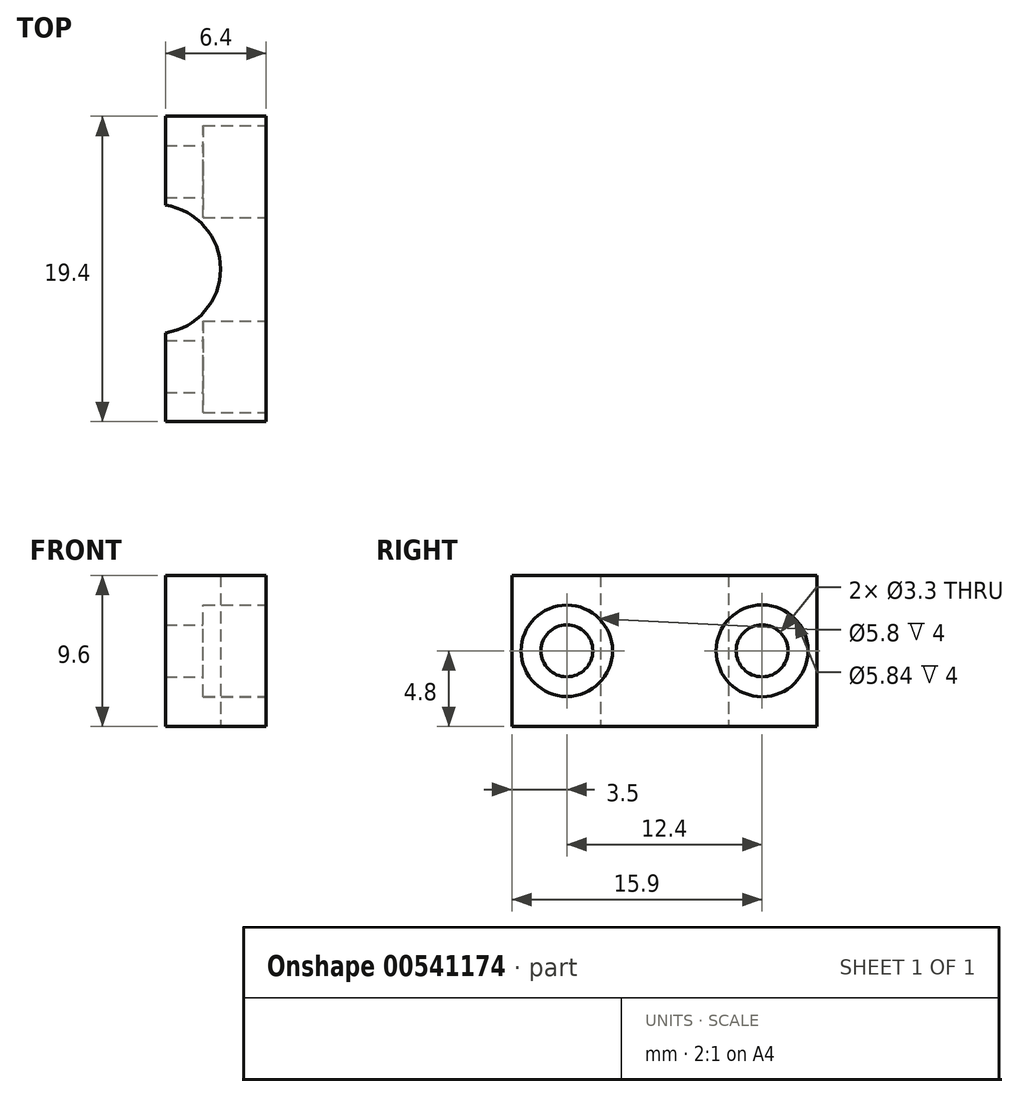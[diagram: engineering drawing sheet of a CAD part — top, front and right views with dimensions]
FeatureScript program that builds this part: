
annotation { "Feature Type Name" : "Feature", "Feature Type Description" : "" }
export const myFeature = defineFeature(function(context is Context, id is Id, definition is map)
    precondition{}
    {
        {
            var Q0;
            Q0=qCreatedBy(makeId("Top.planeOp"),FACE);
            var sketch = newSketch(context, id + "F0", { "sketchPlane" : qUnion([Q0])});
            skCircle(sketch, "E0", {"center": v(-7, 9.7) * mm, "radius": 4.1 * mm});
            skLineSegment(sketch, "E1", {"start": v(-7, 9.7) * mm, "end": v(-7, 35.1) * mm, "construction": true});
            skLineSegment(sketch, "E2", {"start": v(-7.6, 13.76) * mm, "end": v(-7.6, 19.7) * mm});
            skLineSegment(sketch, "E3", {"start": v(-7.6, 19.7) * mm, "end": v(-7, 19.7) * mm});
            skLineSegment(sketch, "E4.MirrorCS", {"start": v(-6.4, 19.7) * mm, "end": v(-7, 19.7) * mm});
            skLineSegment(sketch, "E5.MirrorCS", {"start": v(-6.4, 13.76) * mm, "end": v(-6.4, 19.7) * mm});
            skLineSegment(sketch, "E6", {"start": v(-6.4, 19.7) * mm, "end": v(0, 19.7) * mm});
            skLineSegment(sketch, "E7", {"start": v(0, 19.7) * mm, "end": v(0, 19.4) * mm});
            skLineSegment(sketch, "E8", {"start": v(0, 19.4) * mm, "end": v(-6.4, 19.4) * mm});
            skLineSegment(sketch, "E9", {"start": v(-7, 9.7) * mm, "end": v(-20.13, 9.7) * mm, "construction": true});
            skLineSegment(sketch, "E10.MirrorCS", {"start": v(-6.4, 5.64) * mm, "end": v(-6.4, -0.3) * mm});
            skLineSegment(sketch, "E11.MirrorCS", {"start": v(-7.6, 5.64) * mm, "end": v(-7.6, -0.3) * mm});
            skLineSegment(sketch, "E12.MirrorCS", {"start": v(0, 0) * mm, "end": v(-6.4, 0) * mm});
            skLineSegment(sketch, "E13.MirrorCS", {"start": v(-6.4, -0.3) * mm, "end": v(0, -0.3) * mm});
            skLineSegment(sketch, "E14.MirrorCS", {"start": v(0, -0.3) * mm, "end": v(0, 0) * mm});
            skLineSegment(sketch, "E15.MirrorCS", {"start": v(-6.4, -0.3) * mm, "end": v(-7, -0.3) * mm});
            skLineSegment(sketch, "E16.MirrorCS", {"start": v(-7.6, -0.3) * mm, "end": v(-7, -0.3) * mm});
            skLineSegment(sketch, "E17", {"start": v(0, 0) * mm, "end": v(0, 19.4) * mm});
            skSolve(sketch);
        }
        {
            var Q0;
            {var subQ0=sQuery(id+"F0.wireOp",EDGE,"E8");Q0=makeQuery(id+"F0.imprint","IMPRINT",FACE,{"disambiguationData":[TD([[makeQuery(id+"F0.imprint","IMPRINT",EDGE,{"derivedFrom":subQ0}),1.0]])]});}
            extrude(context, id + "F1", {"entities" : qUnion([Q0]), "depth" : 9.6 * mm, "offsetDistance" : 25 * mm});
        }
        {
            var Q0;
            Q0=qCreatedBy(makeId("Right.planeOp"),FACE);
            var sketch = newSketch(context, id + "F2", { "sketchPlane" : qUnion([Q0])});
            skCircle(sketch, "E18", {"center": v(15.9, 4.8) * mm, "radius": 1.65 * mm});
            skCircle(sketch, "E19", {"center": v(3.5, 4.8) * mm, "radius": 1.65 * mm});
            skPoint(sketch, "E20.0.midPoint", {"position": v(13, 4.8) * mm});
            skPoint(sketch, "E21.0.midPoint", {"position": v(0.6, 4.8) * mm});
            skCircle(sketch, "E22", {"center": v(15.9, 4.8) * mm, "radius": 2.92 * mm});
            skCircle(sketch, "E23", {"center": v(3.5, 4.8) * mm, "radius": 2.9 * mm});
            skSolve(sketch);
        }
        {
            var Q0;
            Q0=makeQuery(id+"F2.imprint","IMPRINT",FACE,{"disambiguationData":[TD([[makeQuery(id+"F2.imprint","IMPRINT",EDGE,{"derivedFrom":sQuery(id+"F2.wireOp",EDGE,"E19")}),1.0]])]});
            var Q1;
            Q1=makeQuery(id+"F2.imprint","IMPRINT",FACE,{"disambiguationData":[TD([[makeQuery(id+"F2.imprint","IMPRINT",EDGE,{"derivedFrom":sQuery(id+"F2.wireOp",EDGE,"E18")}),1.0]])]});
            extrude(context, id + "F3", {"entities" : qUnion([Q0, Q1]), "operationType" : NewBodyOperationType.REMOVE, "oppositeDirection" : true, "depth" : 25 * mm, "offsetDistance" : 25 * mm});
        }
        {
            var Q0;
            Q0=makeQuery(id+"F2.imprint","IMPRINT",FACE,{"disambiguationData":[TD([[makeQuery(id+"F2.imprint","IMPRINT",EDGE,{"derivedFrom":sQuery(id+"F2.wireOp",EDGE,"E19")}),-1.0]])]});
            var Q1;
            Q1=makeQuery(id+"F2.imprint","IMPRINT",FACE,{"disambiguationData":[TD([[makeQuery(id+"F2.imprint","IMPRINT",EDGE,{"derivedFrom":sQuery(id+"F2.wireOp",EDGE,"E18")}),-1.0]])]});
            extrude(context, id + "F4", {"entities" : qUnion([Q0, Q1]), "operationType" : NewBodyOperationType.REMOVE, "oppositeDirection" : true, "depth" : 4 * mm, "offsetDistance" : 25 * mm});
        }
    });
